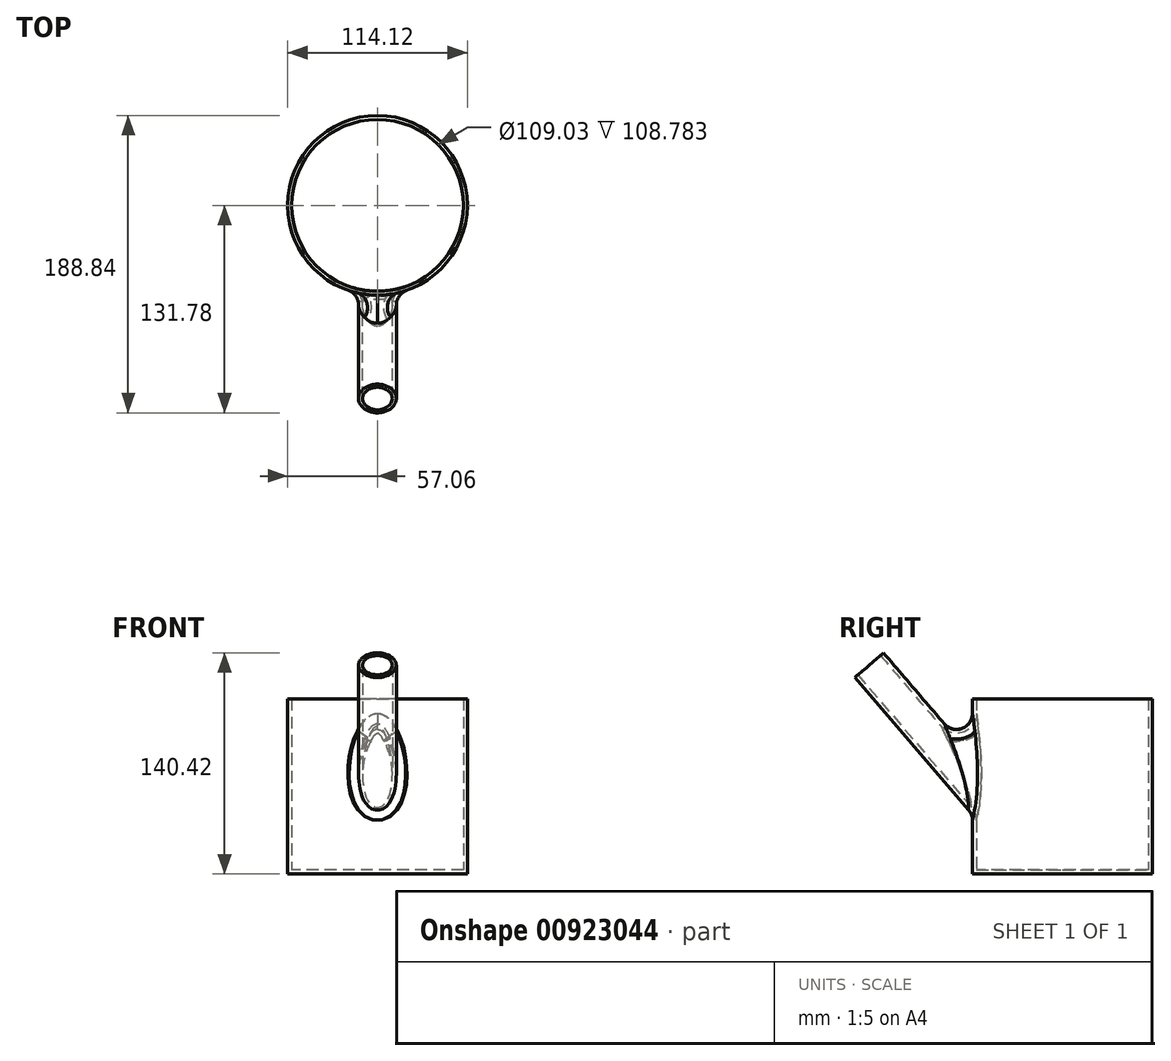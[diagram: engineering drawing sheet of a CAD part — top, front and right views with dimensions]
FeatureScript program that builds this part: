
annotation { "Feature Type Name" : "Feature", "Feature Type Description" : "" }
export const myFeature = defineFeature(function(context is Context, id is Id, definition is map)
    precondition{}
    {
        {
            var Q0;
            Q0=qCreatedBy(makeId("Top.planeOp"),FACE);
            var sketch = newSketch(context, id + "F0", { "sketchPlane" : qUnion([Q0])});
            skCircle(sketch, "E0", {"center": v(0, 0) * mm, "radius": 54.52 * mm});
            skSolve(sketch);
        }
        {
            var Q0;
            Q0 = qSketchRegion(id + "F0", true);
            var Q1;
            Q1=makeQuery(id+"F0.imprint","IMPRINT",FACE,{"disambiguationData":[TD([[makeQuery(id+"F0.imprint","IMPRINT",EDGE,{"derivedFrom":sQuery(id+"F0.wireOp",EDGE,"E0")}),1.0]])]});
            extrude(context, id + "F1", {"entities" : qUnion([Q0, Q1]), "depth" : 108.78 * mm, "offsetDistance" : 25.4 * mm});
        }
        {
            var Q0;
            Q0=qCreatedBy(makeId("Right.planeOp"),FACE);
            var sketch = newSketch(context, id + "F2", { "sketchPlane" : qUnion([Q0])});
            skLineSegment(sketch, "E1", {"start": v(-122.31, 130.4) * mm, "end": v(-41.99, 36.8) * mm});
            skSolve(sketch);
        }
        {
            var Q0;
            Q0=sQuery(id+"F2.wireOp",VERTEX,"E1.start");
            var Q1;
            Q1=sQuery(id+"F2.wireOp",EDGE,"E1");
            cPlane(context, id + "F3", {"entities" : qUnion([Q0, Q1]), "cplaneType" : CPlaneType.LINE_POINT, "offset" : 25.4 * mm, "width" : 152.4 * mm, "height" : 152.4 * mm});
        }
        {
            var Q0;
            Q0=qCreatedBy(id+"F3.planeOp",FACE);
            var sketch = newSketch(context, id + "F4", { "sketchPlane" : qUnion([Q0])});
            skCircle(sketch, "E2", {"center": v(0, 8.4) * mm, "radius": 9.44 * mm});
            skSolve(sketch);
        }
        {
            var Q0;
            Q0=makeQuery(id+"F4.imprint","IMPRINT",FACE,{"disambiguationData":[TD([[makeQuery(id+"F4.imprint","IMPRINT",EDGE,{"derivedFrom":sQuery(id+"F4.wireOp",EDGE,"E2")}),1.0]])]});
            var Q1;
            Q1=sQuery(id+"F2.wireOp",EDGE,"E1");
            sweep(context, id + "F5", {"operationType" : NewBodyOperationType.ADD, "profiles" : qUnion([Q0]), "path" : qUnion([Q1])});
        }
        {
            var Q0;
            Q0=makeQuery(id+"F5.boolean.opBoolean","INTERSECT",EDGE,{"derivedFrom":[makeQuery(id+"F1.opExtrude","SWEPT_FACE",FACE,{"disambiguationData":[OSD([sQuery(id+"F0.wireOp",EDGE,"E0")])]}),makeQuery(id+"F5.opSweep","SWEPT_FACE",FACE,{"disambiguationData":[OSD([sQuery(id+"F2.wireOp",EDGE,"E1"),sQuery(id+"F4.wireOp",EDGE,"E2")])]})]});
            fillet(context, id + "F6", {"entities" : qUnion([Q0]), "radius" : 12.7 * mm, "tangentPropagation" : true, "allowEdgeOverflow" : false});
        }
        {
            var Q0;
            Q0=makeQuery(id+"F1.opExtrude","CAP_FACE",FACE,{"disambiguationData":[OSD([sQuery(id+"F0.wireOp",EDGE,"E0")])],"isStart":false});
            var Q1;
            Q1=makeQuery(id+"F5.opSweep","CAP_FACE",FACE,{"disambiguationData":[OSD([sQuery(id+"F2.wireOp",VERTEX,"E1.start"),sQuery(id+"F4.wireOp",EDGE,"E2")])],"isStart":true});
            shell(context, id + "F7", {"entities" : qUnion([Q0, Q1]), "thickness" : 2.54 * mm, "oppositeDirection" : true});
        }
    });
